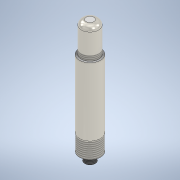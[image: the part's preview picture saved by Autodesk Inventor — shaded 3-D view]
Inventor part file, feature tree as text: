
AUTODESK INVENTOR PART (.ipt)
format: ipt  version: 2020 (Build 240168000, 168)  size: 143,872 bytes
history: native  units: mm
features: extrude x4, sketch x4, thread x3, other x1, fillet x1
ambient origin geometry x8: Origin, YZ Plane, XZ Plane, XY Plane, X Axis, Y Axis, Z Axis, Center Point
bodies: Body1 (feature_tree)
feature tree (13):
  other  "Sólido1"
  extrude  "Extrusión1"  Depth=151.0mm TaperAngle=0.0deg
  extrude  "Extrusión2"  Depth=37.2mm TaperAngle=0.0deg
  fillet  "Empalme1"  Radius=6.0mm
  thread  "Rosca1"  [1 undecoded]
  extrude  "Extrusión3"  Depth=10.0mm TaperAngle=0.0deg
  extrude  "Extrusión4"  Depth=20.0mm TaperAngle=0.0deg
  thread  "Rosca2"  [1 undecoded]
  thread  "Rosca3"  [1 undecoded]
  sketch  "Boceto1"  dims[d0=26.0mm d1=151.0mm d2=0.0mm]
  sketch  "Boceto2"  dims[d3=21.5mm d4=37.2mm d5=0.0mm d6=6.0mm d7=31.2mm d8=25.0mm]
  sketch  "Boceto3"  dims[d9=13.0mm d10=10.0mm d11=0.0mm]
  sketch  "Boceto4"  dims[d12=25.9mm d13=20.0mm d14=0.0mm d15=15.103mm d16=0.0mm d17=25.006mm d18=1.0mm]
note: 3 required parameter values undecoded (feature->parameter linkage not recoverable at this tier; creation-order binding heuristic only, values carry confidence <= 0.55)
